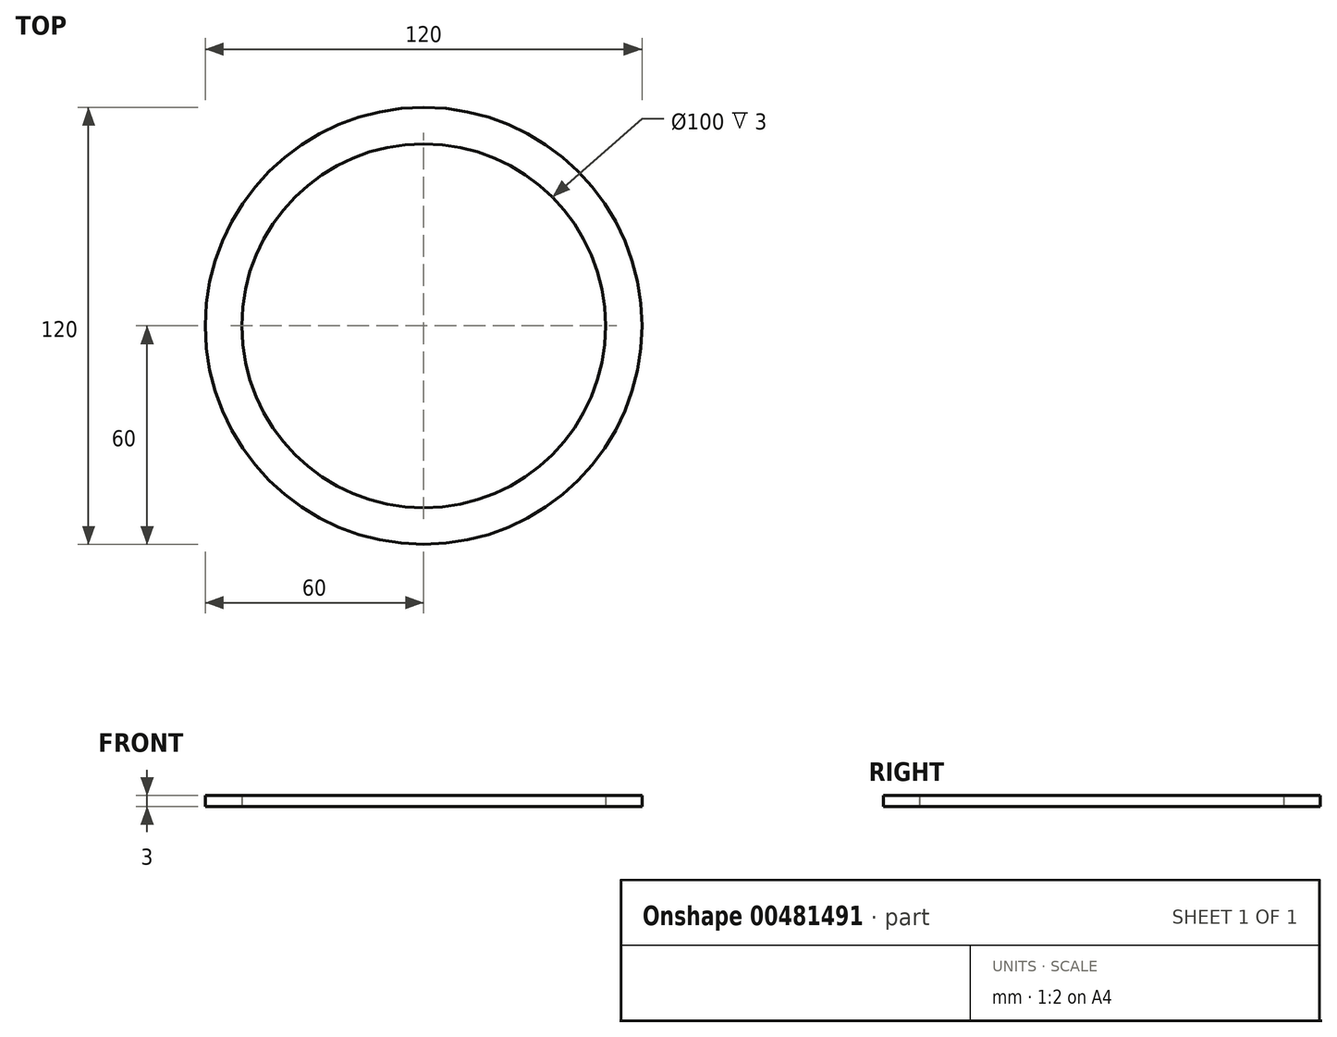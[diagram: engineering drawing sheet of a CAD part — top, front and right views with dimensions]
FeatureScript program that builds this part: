
annotation { "Feature Type Name" : "Feature", "Feature Type Description" : "" }
export const myFeature = defineFeature(function(context is Context, id is Id, definition is map)
    precondition{}
    {
        {
            var Q0;
            Q0=qCreatedBy(makeId("Top.planeOp"),FACE);
            var sketch = newSketch(context, id + "F0", { "sketchPlane" : qUnion([Q0])});
            skCircle(sketch, "E0", {"center": v(0, 0) * mm, "radius": 60 * mm});
            skCircle(sketch, "E1", {"center": v(0, 0) * mm, "radius": 50 * mm});
            skSolve(sketch);
        }
        {
            var Q0;
            Q0 = qSketchRegion(id + "F0", true);
            extrude(context, id + "F1", {"entities" : qUnion([Q0]), "depth" : 3 * mm});
        }
    });
